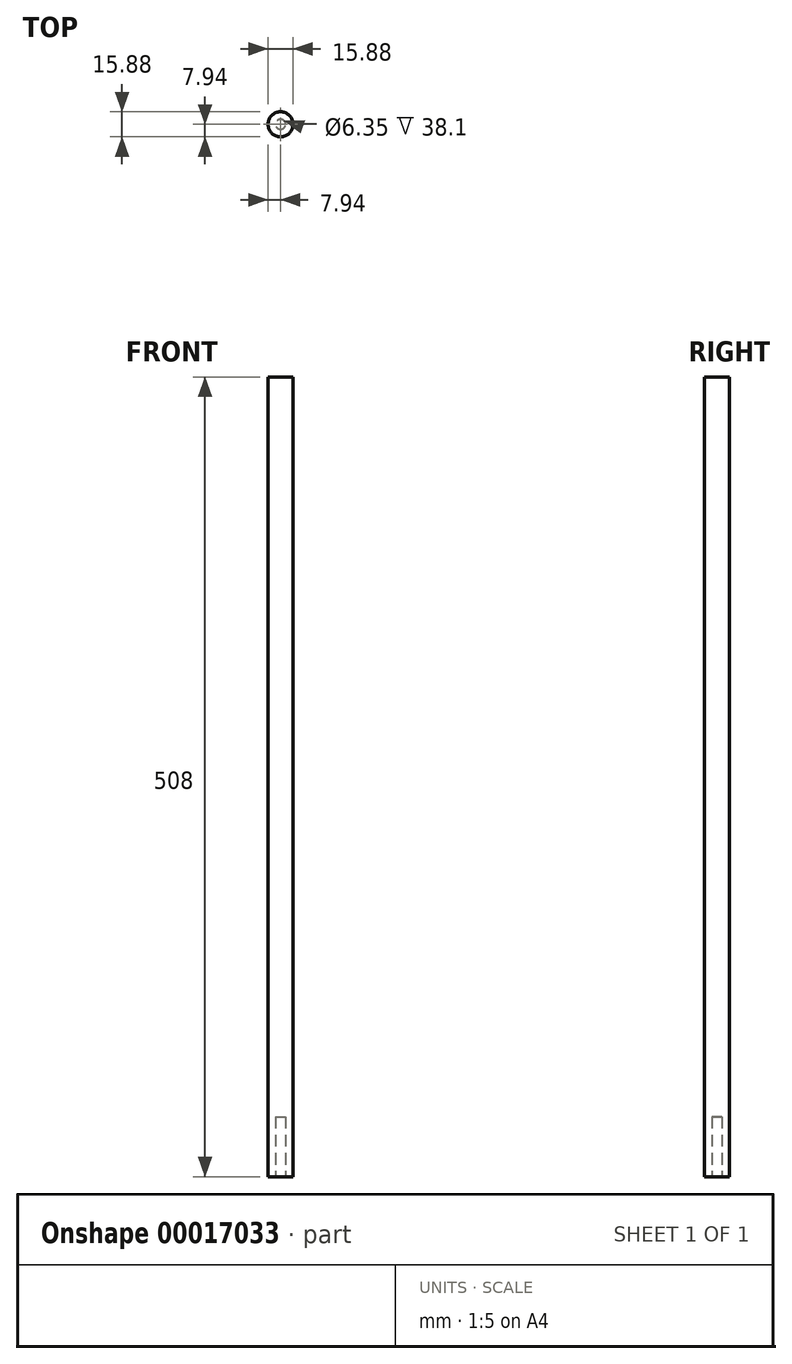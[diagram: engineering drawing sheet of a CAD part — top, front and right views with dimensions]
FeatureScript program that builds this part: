
annotation { "Feature Type Name" : "Feature", "Feature Type Description" : "" }
export const myFeature = defineFeature(function(context is Context, id is Id, definition is map)
    precondition{}
    {
        {
            var Q0;
            Q0=qCreatedBy(makeId("Top.planeOp"),FACE);
            var sketch = newSketch(context, id + "F0", { "sketchPlane" : qUnion([Q0])});
            skCircle(sketch, "E0", {"center": v(0, 0) * mm, "radius": 7.94 * mm});
            skSolve(sketch);
        }
        {
            var Q0;
            Q0 = qSketchRegion(id + "F0", true);
            extrude(context, id + "F1", {"entities" : qUnion([Q0]), "depth" : 508 * mm});
        }
        {
            var Q0;
            Q0=makeQuery(id+"F1.opExtrude","CAP_FACE",FACE,{"disambiguationData":[OSD([sQuery(id+"F0.wireOp",EDGE,"E0")])],"isStart":true});
            var sketch = newSketch(context, id + "F2", { "sketchPlane" : qUnion([Q0])});
            skCircle(sketch, "E1", {"center": v(0, 0) * mm, "radius": 3.18 * mm});
            skSolve(sketch);
        }
        {
            var Q0;
            Q0 = qSketchRegion(id + "F2", true);
            extrude(context, id + "F3", {"entities" : qUnion([Q0]), "operationType" : NewBodyOperationType.REMOVE, "oppositeDirection" : true, "depth" : 38.1 * mm});
        }
    });
